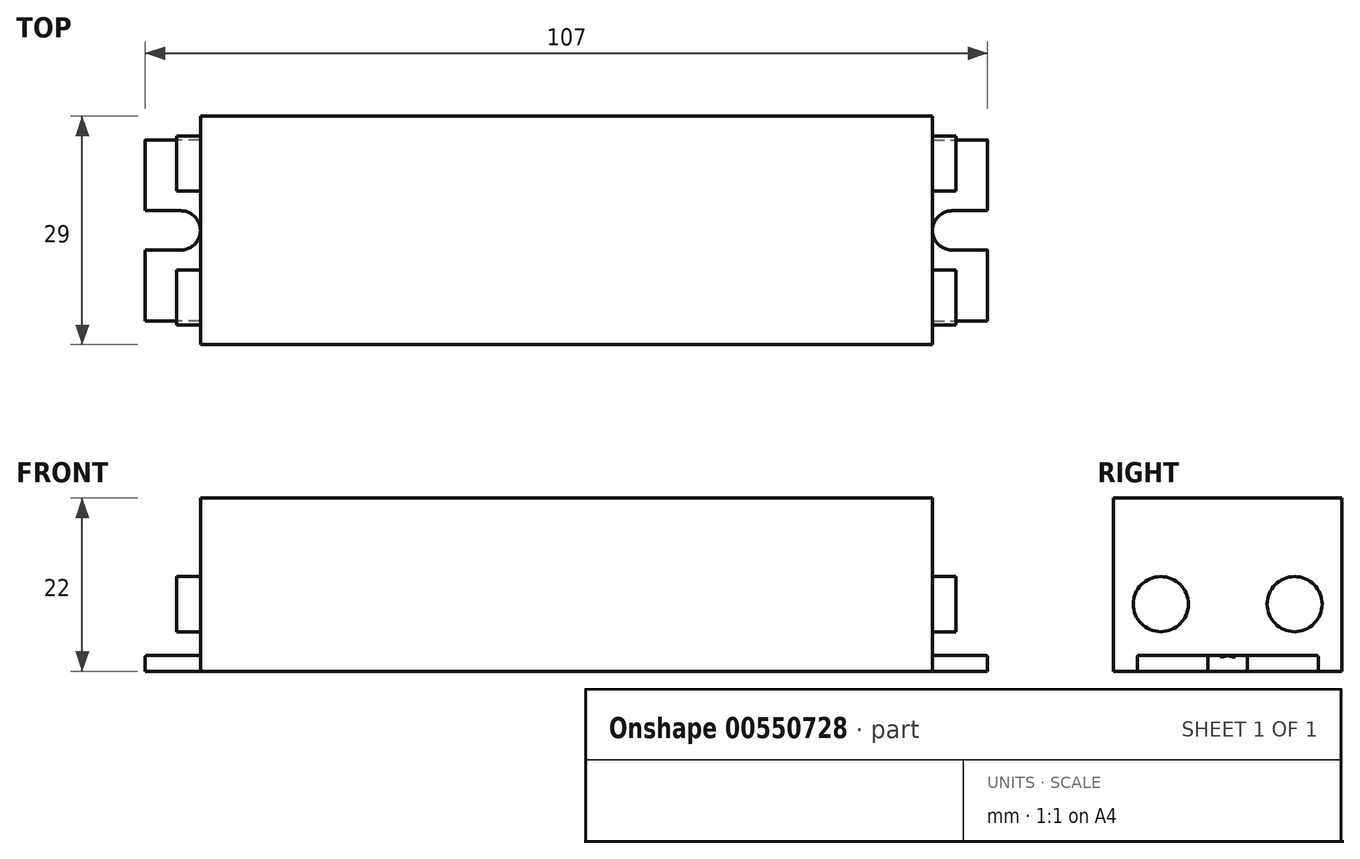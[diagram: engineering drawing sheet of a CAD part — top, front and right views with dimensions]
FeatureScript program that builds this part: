
annotation { "Feature Type Name" : "Feature", "Feature Type Description" : "" }
export const myFeature = defineFeature(function(context is Context, id is Id, definition is map)
    precondition{}
    {
        {
            var Q0;
            Q0=qCreatedBy(makeId("Top.planeOp"),FACE);
            var sketch = newSketch(context, id + "F0", { "sketchPlane" : qUnion([Q0])});
            skLineSegment(sketch, "E0.rect.bottom", {"start": v(-46.5, 14.5) * mm, "end": v(46.5, 14.5) * mm});
            skLineSegment(sketch, "E0.rect.top", {"start": v(-46.5, -14.5) * mm, "end": v(46.5, -14.5) * mm});
            skLineSegment(sketch, "E0.rect.left", {"start": v(-46.5, 14.5) * mm, "end": v(-46.5, -14.5) * mm});
            skLineSegment(sketch, "E0.rect.right", {"start": v(46.5, 14.5) * mm, "end": v(46.5, -14.5) * mm});
            skPoint(sketch, "E0.rect.middle", {"position": v(0, 0) * mm});
            skLineSegment(sketch, "E1", {"start": v(-64.16, 0) * mm, "end": v(77.96, 0) * mm, "construction": true});
            skLineSegment(sketch, "E2", {"start": v(0, 14.5) * mm, "end": v(0, -14.5) * mm, "construction": true});
            skLineSegment(sketch, "E3.bottom", {"start": v(46.5, 11.5) * mm, "end": v(53.5, 11.5) * mm});
            skLineSegment(sketch, "E3.top", {"start": v(46.5, -11.5) * mm, "end": v(53.5, -11.5) * mm});
            skLineSegment(sketch, "E3.left", {"start": v(46.5, 11.5) * mm, "end": v(46.5, -11.5) * mm});
            skLineSegment(sketch, "E3.right", {"start": v(53.5, 11.5) * mm, "end": v(53.5, -11.5) * mm});
            skLineSegment(sketch, "E4", {"start": v(53.5, 11.5) * mm, "end": v(53.5, 14.5) * mm, "construction": true});
            skLineSegment(sketch, "E5", {"start": v(53.5, -11.5) * mm, "end": v(53.5, -14.5) * mm, "construction": true});
            skCircle(sketch, "E6", {"center": v(49, 0) * mm, "radius": 2.5 * mm});
            skLineSegment(sketch, "E7.bottom", {"start": v(49, 2.5) * mm, "end": v(53.5, 2.5) * mm});
            skLineSegment(sketch, "E7.top", {"start": v(49, -2.5) * mm, "end": v(53.5, -2.5) * mm});
            skLineSegment(sketch, "E7.left", {"start": v(49, 2.5) * mm, "end": v(49, -2.5) * mm});
            skLineSegment(sketch, "E7.right", {"start": v(53.5, 2.5) * mm, "end": v(53.5, -2.5) * mm});
            skCircle(sketch, "E8.0.MirrorC", {"center": v(-49, 0) * mm, "radius": 2.5 * mm});
            skLineSegment(sketch, "E9.0.MirrorCS", {"start": v(-49, -2.5) * mm, "end": v(-53.5, -2.5) * mm});
            skLineSegment(sketch, "E10.0.MirrorCS", {"start": v(-49, 2.5) * mm, "end": v(-53.5, 2.5) * mm});
            skLineSegment(sketch, "E11.0.MirrorCS", {"start": v(-46.5, -11.5) * mm, "end": v(-53.5, -11.5) * mm});
            skLineSegment(sketch, "E12.0.MirrorCS", {"start": v(-53.5, 11.5) * mm, "end": v(-53.5, -11.5) * mm});
            skLineSegment(sketch, "E13.0.MirrorCS", {"start": v(-46.5, 11.5) * mm, "end": v(-53.5, 11.5) * mm});
            skSolve(sketch);
        }
        {
            var Q0;
            {var subQ5=sQuery(id+"F0.wireOp",EDGE,"E0.rect.bottom");Q0=makeQuery(id+"F0.imprint","IMPRINT",FACE,{"disambiguationData":[TD([[makeQuery(id+"F0.imprint","IMPRINT",EDGE,{"derivedFrom":subQ5}),-1.0]])]});}
            extrude(context, id + "F1", {"entities" : qUnion([Q0]), "depth" : 22 * mm});
        }
        {
            var Q0;
            {var subQ5=sQuery(id+"F0.wireOp",EDGE,"E3.top");Q0=makeQuery(id+"F0.imprint","IMPRINT",FACE,{"disambiguationData":[TD([[makeQuery(id+"F0.imprint","IMPRINT",EDGE,{"derivedFrom":subQ5}),1.0]])]});}
            var Q1;
            {var subQ5=sQuery(id+"F0.wireOp",EDGE,"E3.bottom");Q1=makeQuery(id+"F0.imprint","IMPRINT",FACE,{"disambiguationData":[TD([[makeQuery(id+"F0.imprint","IMPRINT",EDGE,{"derivedFrom":subQ5}),-1.0]])]});}
            var Q2;
            {var subQ2=sQuery(id+"F0.wireOp",EDGE,"E9.0.MirrorCS");Q2=makeQuery(id+"F0.imprint","IMPRINT",FACE,{"disambiguationData":[TD([[makeQuery(id+"F0.imprint","IMPRINT",EDGE,{"derivedFrom":subQ2}),1.0]])]});}
            var Q3;
            {var subQ2=sQuery(id+"F0.wireOp",EDGE,"E10.0.MirrorCS");Q3=makeQuery(id+"F0.imprint","IMPRINT",FACE,{"disambiguationData":[TD([[makeQuery(id+"F0.imprint","IMPRINT",EDGE,{"derivedFrom":subQ2}),-1.0]])]});}
            extrude(context, id + "F2", {"entities" : qUnion([Q0, Q1, Q2, Q3]), "operationType" : NewBodyOperationType.ADD, "depth" : 2 * mm});
        }
        {
            var Q0;
            Q0=makeQuery(id+"F2.opExtrude","CAP_EDGE",EDGE,{"disambiguationData":[OSD([sQuery(id+"F0.wireOp",EDGE,"E9.0.MirrorCS")])],"isStart":false});
            var Q1;
            {var subQ0=sQuery(id+"F0.wireOp",EDGE,"E8.0.MirrorC");Q1=makeQuery(id+"F2.opExtrude","CAP_EDGE",EDGE,{"disambiguationData":[OSD([subQ0]),TDD([makeQuery(id+"F0.imprint","IMPRINT",EDGE,{"disambiguationData":[TD([[makeQuery(id+"F0.imprint","INTERSECT",VERTEX,{"derivedFrom":[subQ0,sQuery(id+"F0.wireOp",EDGE,"E9.0.MirrorCS")]}),1.0]])],"derivedFrom":subQ0})])],"isStart":false});}
            var Q2;
            {var subQ0=sQuery(id+"F0.wireOp",EDGE,"E8.0.MirrorC");Q2=makeQuery(id+"F2.opExtrude","CAP_EDGE",EDGE,{"disambiguationData":[OSD([subQ0]),TDD([makeQuery(id+"F0.imprint","IMPRINT",EDGE,{"disambiguationData":[TD([[makeQuery(id+"F0.imprint","INTERSECT",VERTEX,{"derivedFrom":[subQ0,sQuery(id+"F0.wireOp",EDGE,"E10.0.MirrorCS")]}),-1.0]])],"derivedFrom":subQ0})])],"isStart":false});}
            var Q3;
            Q3=makeQuery(id+"F2.opExtrude","CAP_EDGE",EDGE,{"disambiguationData":[OSD([sQuery(id+"F0.wireOp",EDGE,"E10.0.MirrorCS")])],"isStart":false});
            var Q4;
            {var subQ0=sQuery(id+"F0.wireOp",EDGE,"E12.0.MirrorCS");Q4=makeQuery(id+"F2.opExtrude","CAP_EDGE",EDGE,{"disambiguationData":[OSD([subQ0]),TDD([makeQuery(id+"F0.imprint","IMPRINT",EDGE,{"disambiguationData":[TD([[makeQuery(id+"F0.imprint","INTERSECT",VERTEX,{"derivedFrom":[sQuery(id+"F0.wireOp",EDGE,"E9.0.MirrorCS"),subQ0]}),-1.0]])],"derivedFrom":subQ0})])],"isStart":false});}
            var Q5;
            Q5=makeQuery(id+"F2.opExtrude","CAP_EDGE",EDGE,{"disambiguationData":[OSD([sQuery(id+"F0.wireOp",EDGE,"E11.0.MirrorCS")])],"isStart":false});
            var Q6;
            {var subQ0=sQuery(id+"F0.wireOp",EDGE,"E12.0.MirrorCS");Q6=makeQuery(id+"F2.opExtrude","CAP_EDGE",EDGE,{"disambiguationData":[OSD([subQ0]),TDD([makeQuery(id+"F0.imprint","IMPRINT",EDGE,{"disambiguationData":[TD([[makeQuery(id+"F0.imprint","INTERSECT",VERTEX,{"derivedFrom":[sQuery(id+"F0.wireOp",EDGE,"E10.0.MirrorCS"),subQ0]}),1.0]])],"derivedFrom":subQ0})])],"isStart":false});}
            var Q7;
            Q7=makeQuery(id+"F2.opExtrude","CAP_EDGE",EDGE,{"disambiguationData":[OSD([sQuery(id+"F0.wireOp",EDGE,"E13.0.MirrorCS")])],"isStart":false});
            var Q8;
            Q8=makeQuery(id+"F2.opExtrude","CAP_EDGE",EDGE,{"disambiguationData":[OSD([sQuery(id+"F0.wireOp",EDGE,"E3.top")])],"isStart":false});
            var Q9;
            {var subQ0=sQuery(id+"F0.wireOp",EDGE,"E3.right");Q9=makeQuery(id+"F2.opExtrude","CAP_EDGE",EDGE,{"disambiguationData":[OSD([subQ0]),TDD([makeQuery(id+"F0.imprint","IMPRINT",EDGE,{"disambiguationData":[TD([[makeQuery(id+"F0.imprint","INTERSECT",VERTEX,{"derivedFrom":[sQuery(id+"F0.wireOp",EDGE,"E3.top"),subQ0]}),1.0]])],"derivedFrom":subQ0})])],"isStart":false});}
            var Q10;
            Q10=makeQuery(id+"F2.opExtrude","CAP_EDGE",EDGE,{"disambiguationData":[OSD([sQuery(id+"F0.wireOp",EDGE,"E7.top")])],"isStart":false});
            var Q11;
            {var subQ0=sQuery(id+"F0.wireOp",EDGE,"E6");Q11=makeQuery(id+"F2.opExtrude","CAP_EDGE",EDGE,{"disambiguationData":[OSD([subQ0]),TDD([makeQuery(id+"F0.imprint","IMPRINT",EDGE,{"disambiguationData":[TD([[makeQuery(id+"F0.imprint","INTERSECT",VERTEX,{"derivedFrom":[sQuery(id+"F0.wireOp",EDGE,"E3.left"),subQ0]}),-1.0]])],"derivedFrom":subQ0})])],"isStart":false});}
            var Q12;
            {var subQ0=sQuery(id+"F0.wireOp",EDGE,"E6");Q12=makeQuery(id+"F2.opExtrude","CAP_EDGE",EDGE,{"disambiguationData":[OSD([subQ0]),TDD([makeQuery(id+"F0.imprint","IMPRINT",EDGE,{"disambiguationData":[TD([[makeQuery(id+"F0.imprint","INTERSECT",VERTEX,{"derivedFrom":[sQuery(id+"F0.wireOp",EDGE,"E3.left"),subQ0]}),1.0]])],"derivedFrom":subQ0})])],"isStart":false});}
            var Q13;
            Q13=makeQuery(id+"F2.opExtrude","CAP_EDGE",EDGE,{"disambiguationData":[OSD([sQuery(id+"F0.wireOp",EDGE,"E7.bottom")])],"isStart":false});
            var Q14;
            {var subQ0=sQuery(id+"F0.wireOp",EDGE,"E3.right");Q14=makeQuery(id+"F2.opExtrude","CAP_EDGE",EDGE,{"disambiguationData":[OSD([subQ0]),TDD([makeQuery(id+"F0.imprint","IMPRINT",EDGE,{"disambiguationData":[TD([[makeQuery(id+"F0.imprint","INTERSECT",VERTEX,{"derivedFrom":[sQuery(id+"F0.wireOp",EDGE,"E3.bottom"),subQ0]}),-1.0]])],"derivedFrom":subQ0})])],"isStart":false});}
            var Q15;
            Q15=makeQuery(id+"F2.opExtrude","CAP_EDGE",EDGE,{"disambiguationData":[OSD([sQuery(id+"F0.wireOp",EDGE,"E3.bottom")])],"isStart":false});
            fillet(context, id + "F3", {"entities" : qUnion([Q0, Q1, Q2, Q3, Q4, Q5, Q6, Q7, Q8, Q9, Q10, Q11, Q12, Q13, Q14, Q15]), "radius" : 0.2 * mm, "tangentPropagation" : true, "allowEdgeOverflow" : false});
        }
        {
            var Q0;
            Q0=makeQuery(id+"F1.opExtrude","SWEPT_FACE",FACE,{"disambiguationData":[OSD([sQuery(id+"F0.wireOp",EDGE,"E0.rect.right"),sQuery(id+"F0.wireOp",EDGE,"E3.left")])]});
            var sketch = newSketch(context, id + "F4", { "sketchPlane" : qUnion([Q0])});
            skLineSegment(sketch, "E14", {"start": v(0, 22) * mm, "end": v(0, 0) * mm, "construction": true});
            skCircle(sketch, "E15", {"center": v(-8.5, 8.52) * mm, "radius": 3.5 * mm});
            skCircle(sketch, "E16.0.MirrorC", {"center": v(8.5, 8.52) * mm, "radius": 3.5 * mm});
            skSolve(sketch);
        }
        {
            var Q0;
            Q0=qSketchRegion(id+"F4",true);
            extrude(context, id + "F5", {"entities" : qUnion([Q0]), "operationType" : NewBodyOperationType.ADD, "depth" : 3 * mm, "hasSecondDirection" : true, "secondDirectionOppositeDirection" : true, "secondDirectionDepth" : 96 * mm});
        }
    });
